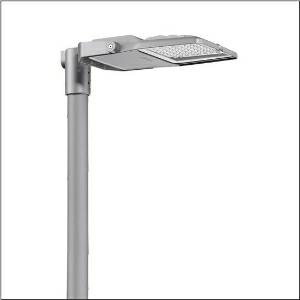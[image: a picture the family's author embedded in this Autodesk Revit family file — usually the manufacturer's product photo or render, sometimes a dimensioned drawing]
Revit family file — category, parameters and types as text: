
# Revit family: floodlight_fl_21_iq_mini___pl33t_5xa7772d2f3a_d038
name_source: partatom
category: Lighting Fixtures
units: mm (PartAtom-declared; Revit-internal decimal feet)

## family parameters
Cut with Voids When Loaded = No
Host = Face
Light Source = No
Part Type = Normal
Room Calculation Point = No
Round Connector Dimension = Use Diameter
Shared = No

## types (1)
- --- (1 x LED, 17620 lm, 143 W, 3000K)
    Apparent Load = 143 VA
    CIE Flux Codes = 26 75 99 100 100
    Color Rendering = 70
    Color Temperature = 3000K
    Default Elevation = 1800 mm
    Description = Floodlight FL 21 iQ mini, floodlight, primary light control with lens, of PMMA, primary optical cover: protective disc, of toughened safety glass, transparent, light distribution: PL33T, light emission: direct distribution, installation type: surface-mounted, LED, High Power LED, rated luminous flux: 17.620lm, luminous efficacy: 123lm/W, light colour: 730, colour temperature: 3000K, control gear: iQ Street-Remote/DALI, control: Auto-Match, Temp-Guard, Night-Set, Smart-Wire, Desk-Remote (wireless, voltage-free reading and setting of iQ features in the workshop via application-optimized NFC function/RFID function), optimised constant luminous flux control (CLO 2.0), Light-Fading, Lumen-Switch, with terminal, 6-pole, mains connection: 220..240V, AC, 50/60Hz, start of lifetime: 143W, end of service life: 152W, reduction: 61W, luminaire housing, of diecast aluminium, powder-coated, Siteco® metallic grey (DB 702S), corrosivity category C5 mid according to DIN EN ISO 12944, suitable for swimming pools, chlorine-resistant, sealing non-destructively replaceable, please order mast flange separately, mast bracket, of steel, galvanised, powder-coated, protection rating (complete): IP66, insulation class (complete): insulation class II (safety insulation), certification: CE, ENEC, VDE, protection symbol: D, impact resistance: IK08, permissible operating ambient temperature: -40..+40°C, permissible operating ambient temperature for outdoor applications: -40..+50°C, standard: DIN EN 12944, LABS conformity tested according to VDMA 24364:2018-05, packaging unit: 1 piece

Light Distribution: PL33T
    Height = 70 mm
    Lamp = 1 x LED
    Lamp Light Flux = 17620 lm
    Lamp Power = 143 W
    Lamp count = 1
    Length = 485 mm
    Luminous efficacy = 123 lm/W
    Manufacturer = Siteco
    ModVariant = No
    Model = 5XA7772D2F3A
    Number of Poles = 1
    OnlyDefault = Yes
    Power Factor = 1
    Product Name = Floodlight FL 21 iQ mini | PL33T
    Product group = floodlight | pylon annexe
    ProductGroupID = 6201
    Protection Class = Protection class II
    Protection Degree = IP 66
    RLX_Detail_Level = 1
    RLX_Emergency_Light_Flux = 0 lm
    RLX_Emergency_Type = 0
    RLX_Emergency_Type_DB = No
    RlxData = <blob elided: 101505 chars, md5=2be38d26>
    Socket = socket
    Standby Power = 0 W
    System Light Flux = 17620 lm
    System Power = 143 W
    Type Comments = factory setting: luminous flux: 100 % | dim-lin: 254 | 730 mA
    Type Image = l_1007125.jpg
    URL = http://relux.com
    VarID = @adj_170373
    Voltage = 0 V
    Weight = 0.00 kg
    Width = 337 mm

## geometry (parser evidence)
native form markers: Blend x4, Sweep x13
no freeform markers — native parametric forms only
